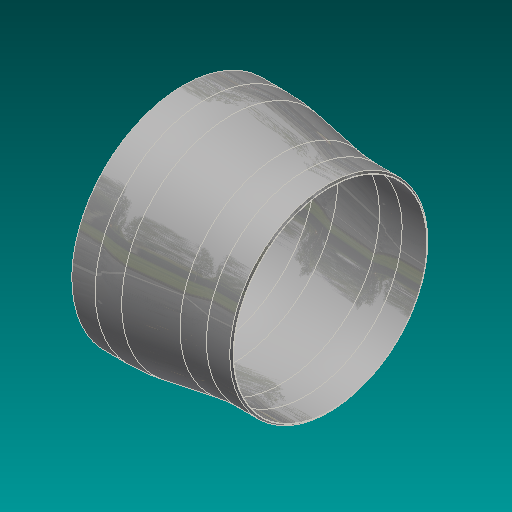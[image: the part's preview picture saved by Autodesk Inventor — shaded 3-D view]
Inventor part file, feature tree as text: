
AUTODESK INVENTOR PART (.ipt)
format: ipt  version: 2017.3 (Build 213256000, 256)  size: 243,200 bytes
history: native  units: in
note: dims shown in document units (in); Inventor stores cm internally (conversion verified against a paired STEP export)
features: fillet x3, chamfer x2, revolve x1, sketch x1
ambient origin geometry x8: Origin, YZ Plane, XZ Plane, XY Plane, X Axis, Y Axis, Z Axis, Center Point
bodies: Solid1 (feature_tree)
feature tree (7):
  revolve  "Revolution1"  [1 undecoded]
  fillet  "Fillet1"  Radius=36.0in
  fillet  "Fillet2"  Radius=32.0in
  fillet  "Fillet3"  Radius=0.375in
  chamfer  "Chamfer1"  Distance=0.375in
  chamfer  "Chamfer2"  Angle=90.0deg  [1 undecoded]
  sketch  "Sketch1"  dims[d0=24.0in d1=6.0in d2=36.0in d3=32.0in d4=0.375in d5=0.375in d6=90.0deg d7=24.0in d8=23.625in d9=24.375in d10=0.3125in d11=0.125in d12=0.2577in d13=0.3125in d14=0.125in d15=0.2577in]
note: 2 required parameter values undecoded (feature->parameter linkage not recoverable at this tier; creation-order binding heuristic only, values carry confidence <= 0.55)